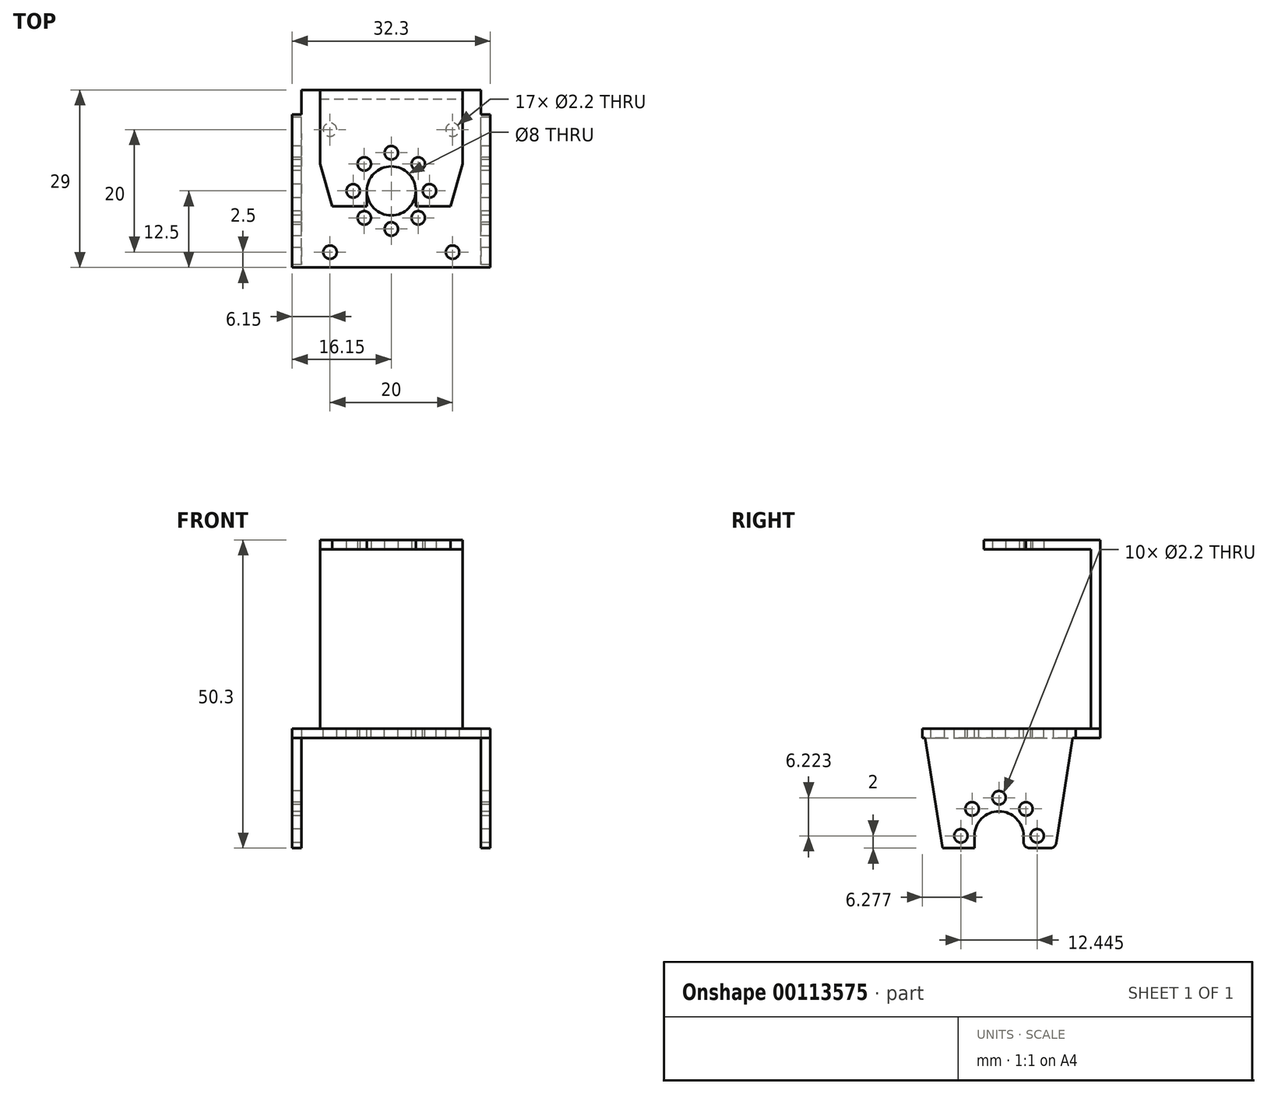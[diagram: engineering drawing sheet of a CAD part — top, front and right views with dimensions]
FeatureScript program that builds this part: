
annotation { "Feature Type Name" : "Feature", "Feature Type Description" : "" }
export const myFeature = defineFeature(function(context is Context, id is Id, definition is map)
    precondition{}
    {
        {
            var Q0;
            Q0=qCreatedBy(makeId("Front.planeOp"),FACE);
            var sketch = newSketch(context, id + "F0", { "sketchPlane" : qUnion([Q0])});
            skLineSegment(sketch, "E0.bottom", {"start": v(0, 0) * mm, "end": v(1.5, 0) * mm});
            skLineSegment(sketch, "E0.top", {"start": v(0, 19.5) * mm, "end": v(32.3, 19.5) * mm});
            skLineSegment(sketch, "E0.left", {"start": v(0, 0) * mm, "end": v(0, 19.5) * mm});
            skLineSegment(sketch, "E0.right", {"start": v(32.3, 0) * mm, "end": v(32.3, 19.5) * mm});
            skLineSegment(sketch, "E1.top", {"start": v(1.5, 18) * mm, "end": v(30.8, 18) * mm});
            skLineSegment(sketch, "E1.left", {"start": v(1.5, 0) * mm, "end": v(1.5, 18) * mm});
            skLineSegment(sketch, "E1.right", {"start": v(30.8, 0) * mm, "end": v(30.8, 18) * mm});
            skLineSegment(sketch, "E2.trimOffspring", {"start": v(30.8, 0) * mm, "end": v(32.3, 0) * mm});
            skSolve(sketch);
        }
        {
            var Q0;
            Q0=qSketchRegion(id+"F0",true);
            extrude(context, id + "F1", {"entities" : qUnion([Q0]), "depth" : 25 * mm});
        }
        {
            var Q0;
            Q0=makeQuery(id+"F1.opExtrude","SWEPT_FACE",FACE,{"disambiguationData":[OSD([sQuery(id+"F0.wireOp",EDGE,"E0.left")])]});
            var sketch = newSketch(context, id + "F2", { "sketchPlane" : qUnion([Q0])});
            skArc(sketch, "E3", {"start": v(16.5, 2) * mm, "mid": v(12.5, 6) * mm, "end": v(8.5, 2) * mm});
            skCircle(sketch, "E4", {"center": v(18.72, 2) * mm, "radius": 1.1 * mm});
            skCircle(sketch, "E5.1.0", {"center": v(16.9, 6.4) * mm, "radius": 1.1 * mm});
            skCircle(sketch, "E5.2.0", {"center": v(12.5, 8.22) * mm, "radius": 1.1 * mm});
            skCircle(sketch, "E5.3.0", {"center": v(8.1, 6.4) * mm, "radius": 1.1 * mm});
            skCircle(sketch, "E5.4.0", {"center": v(6.28, 2) * mm, "radius": 1.1 * mm});
            skLineSegment(sketch, "E6", {"start": v(8.5, 2) * mm, "end": v(8.5, 0) * mm});
            skLineSegment(sketch, "E7", {"start": v(16.5, 2) * mm, "end": v(16.5, 0) * mm});
            skLineSegment(sketch, "E8", {"start": v(8.5, 0) * mm, "end": v(16.5, 0) * mm});
            skLineSegment(sketch, "E9", {"start": v(12.5, 19.5) * mm, "end": v(12.5, 0) * mm, "construction": true});
            skPoint(sketch, "E10", {"position": v(12.5, 0) * mm});
            skLineSegment(sketch, "E11", {"start": v(3.28, 0) * mm, "end": v(0.47, 18) * mm});
            skLineSegment(sketch, "E12", {"start": v(3.28, 0) * mm, "end": v(0, 0) * mm});
            skLineSegment(sketch, "E13", {"start": v(0, 0) * mm, "end": v(0, 18) * mm});
            skLineSegment(sketch, "E14.MirrorCS", {"start": v(25, 0) * mm, "end": v(25, 18) * mm});
            skLineSegment(sketch, "E15.MirrorCS", {"start": v(21.72, 0) * mm, "end": v(24.53, 18) * mm});
            skLineSegment(sketch, "E16.MirrorCS", {"start": v(21.72, 0) * mm, "end": v(25, 0) * mm});
            skLineSegment(sketch, "E17", {"start": v(0, 18) * mm, "end": v(0.47, 18) * mm});
            skPoint(sketch, "E18.orphan", {"position": v(0, 21) * mm});
            skLineSegment(sketch, "E19.MirrorCS", {"start": v(25, 18) * mm, "end": v(24.53, 18) * mm});
            skPoint(sketch, "E20.orphan", {"position": v(25, 21) * mm});
            skSolve(sketch);
        }
        {
            var Q0;
            Q0=qSketchRegion(id+"F2",true);
            extrude(context, id + "F3", {"entities" : qUnion([Q0]), "operationType" : NewBodyOperationType.REMOVE, "endBound" : BoundingType.THROUGH_ALL, "oppositeDirection" : true, "depth" : 25 * mm});
        }
        {
            var Q0;
            Q0=makeQuery(id+"F1.opExtrude","SWEPT_FACE",FACE,{"disambiguationData":[OSD([sQuery(id+"F0.wireOp",EDGE,"E0.top")])]});
            var sketch = newSketch(context, id + "F4", { "sketchPlane" : qUnion([Q0])});
            skLineSegment(sketch, "E21", {"start": v(16.15, 0) * mm, "end": v(16.15, -25) * mm, "construction": true});
            skLineSegment(sketch, "E22", {"start": v(0, -12.5) * mm, "end": v(32.3, -12.5) * mm, "construction": true});
            skCircle(sketch, "E23", {"center": v(6.15, -2.5) * mm, "radius": 1.1 * mm});
            skCircle(sketch, "E24.MirrorC", {"center": v(26.15, -2.5) * mm, "radius": 1.1 * mm});
            skCircle(sketch, "E25.MirrorC", {"center": v(6.15, -22.5) * mm, "radius": 1.1 * mm});
            skCircle(sketch, "E26.MirrorC", {"center": v(26.15, -22.5) * mm, "radius": 1.1 * mm});
            skCircle(sketch, "E27", {"center": v(16.15, -12.5) * mm, "radius": 4 * mm});
            skLineSegment(sketch, "E28.bottom", {"start": v(20.55, -16.9) * mm, "end": v(11.75, -16.9) * mm, "construction": true});
            skLineSegment(sketch, "E28.top", {"start": v(20.55, -8.1) * mm, "end": v(11.75, -8.1) * mm, "construction": true});
            skLineSegment(sketch, "E28.left", {"start": v(20.55, -16.9) * mm, "end": v(20.55, -8.1) * mm, "construction": true});
            skLineSegment(sketch, "E28.right", {"start": v(11.75, -16.9) * mm, "end": v(11.75, -8.1) * mm, "construction": true});
            skCircle(sketch, "E29", {"center": v(11.75, -8.1) * mm, "radius": 1.1 * mm});
            skCircle(sketch, "E30.1.0", {"center": v(9.93, -12.5) * mm, "radius": 1.1 * mm});
            skCircle(sketch, "E30.2.0", {"center": v(11.75, -16.9) * mm, "radius": 1.1 * mm});
            skCircle(sketch, "E30.3.0", {"center": v(16.15, -18.72) * mm, "radius": 1.1 * mm});
            skCircle(sketch, "E31.1.4.0", {"center": v(20.55, -16.9) * mm, "radius": 1.1 * mm});
            skCircle(sketch, "E31.1.5.0", {"center": v(22.37, -12.5) * mm, "radius": 1.1 * mm});
            skCircle(sketch, "E31.1.6.0", {"center": v(20.55, -8.1) * mm, "radius": 1.1 * mm});
            skCircle(sketch, "E31.1.7.0", {"center": v(16.15, -6.28) * mm, "radius": 1.1 * mm});
            skLineSegment(sketch, "E32.0", {"start": v(0, -25) * mm, "end": v(0, 0) * mm, "construction": true});
            skLineSegment(sketch, "E33.0", {"start": v(32.3, -25) * mm, "end": v(32.3, -0.23) * mm, "construction": true});
            skLineSegment(sketch, "E34.0", {"start": v(0, -25) * mm, "end": v(32.3, -25) * mm, "construction": true});
            skPoint(sketch, "E35", {"position": v(16.15, -25) * mm});
            skPoint(sketch, "E36", {"position": v(16.15, 0) * mm});
            skSolve(sketch);
        }
        {
            var Q0;
            Q0=qSketchRegion(id+"F4",true);
            extrude(context, id + "F5", {"entities" : qUnion([Q0]), "operationType" : NewBodyOperationType.REMOVE, "endBound" : BoundingType.UP_TO_NEXT, "oppositeDirection" : true, "depth" : 25 * mm});
        }
        {
            var Q0;
            Q0=makeQuery(id+"F3.boolean.opBoolean","COPY",EDGE,{"disambiguationData":[OD(0.0)],"derivedFrom":makeQuery(id+"F3.opExtrude","SWEPT_EDGE",EDGE,{"disambiguationData":[OSD([sQuery(id+"F0.wireOp",EDGE,"E0.bottom"),sQuery(id+"F0.wireOp",EDGE,"E0.left"),sQuery(id+"F2.wireOp",EDGE,"E11"),sQuery(id+"F2.wireOp",EDGE,"E12")])]})});
            var Q1;
            Q1=makeQuery(id+"F3.boolean.opBoolean","COPY",EDGE,{"disambiguationData":[OD(0.0)],"derivedFrom":makeQuery(id+"F3.opExtrude","SWEPT_EDGE",EDGE,{"disambiguationData":[OSD([sQuery(id+"F0.wireOp",EDGE,"E0.bottom"),sQuery(id+"F0.wireOp",EDGE,"E0.left"),sQuery(id+"F2.wireOp",EDGE,"E6"),sQuery(id+"F2.wireOp",EDGE,"E8")])]})});
            var Q2;
            Q2=makeQuery(id+"F3.boolean.opBoolean","COPY",EDGE,{"disambiguationData":[OD(0.0)],"derivedFrom":makeQuery(id+"F3.opExtrude","SWEPT_EDGE",EDGE,{"disambiguationData":[OSD([sQuery(id+"F0.wireOp",EDGE,"E0.bottom"),sQuery(id+"F0.wireOp",EDGE,"E0.left"),sQuery(id+"F2.wireOp",EDGE,"E7"),sQuery(id+"F2.wireOp",EDGE,"E8")])]})});
            var Q3;
            Q3=makeQuery(id+"F3.boolean.opBoolean","COPY",EDGE,{"disambiguationData":[OD(0.0)],"derivedFrom":makeQuery(id+"F3.opExtrude","SWEPT_EDGE",EDGE,{"disambiguationData":[OSD([sQuery(id+"F0.wireOp",EDGE,"E0.bottom"),sQuery(id+"F0.wireOp",EDGE,"E0.left"),sQuery(id+"F2.wireOp",EDGE,"E15.MirrorCS"),sQuery(id+"F2.wireOp",EDGE,"E16.MirrorCS")])]})});
            var Q4;
            Q4=makeQuery(id+"F3.boolean.opBoolean","COPY",EDGE,{"disambiguationData":[OD(1.0)],"derivedFrom":makeQuery(id+"F3.opExtrude","SWEPT_EDGE",EDGE,{"disambiguationData":[OSD([sQuery(id+"F0.wireOp",EDGE,"E0.bottom"),sQuery(id+"F0.wireOp",EDGE,"E0.left"),sQuery(id+"F2.wireOp",EDGE,"E11"),sQuery(id+"F2.wireOp",EDGE,"E12")])]})});
            var Q5;
            Q5=makeQuery(id+"F3.boolean.opBoolean","COPY",EDGE,{"disambiguationData":[OD(1.0)],"derivedFrom":makeQuery(id+"F3.opExtrude","SWEPT_EDGE",EDGE,{"disambiguationData":[OSD([sQuery(id+"F0.wireOp",EDGE,"E0.bottom"),sQuery(id+"F0.wireOp",EDGE,"E0.left"),sQuery(id+"F2.wireOp",EDGE,"E6"),sQuery(id+"F2.wireOp",EDGE,"E8")])]})});
            var Q6;
            Q6=makeQuery(id+"F3.boolean.opBoolean","COPY",EDGE,{"disambiguationData":[OD(1.0)],"derivedFrom":makeQuery(id+"F3.opExtrude","SWEPT_EDGE",EDGE,{"disambiguationData":[OSD([sQuery(id+"F0.wireOp",EDGE,"E0.bottom"),sQuery(id+"F0.wireOp",EDGE,"E0.left"),sQuery(id+"F2.wireOp",EDGE,"E7"),sQuery(id+"F2.wireOp",EDGE,"E8")])]})});
            var Q7;
            Q7=makeQuery(id+"F3.boolean.opBoolean","COPY",EDGE,{"disambiguationData":[OD(1.0)],"derivedFrom":makeQuery(id+"F3.opExtrude","SWEPT_EDGE",EDGE,{"disambiguationData":[OSD([sQuery(id+"F0.wireOp",EDGE,"E0.bottom"),sQuery(id+"F0.wireOp",EDGE,"E0.left"),sQuery(id+"F2.wireOp",EDGE,"E15.MirrorCS"),sQuery(id+"F2.wireOp",EDGE,"E16.MirrorCS")])]})});
            fillet(context, id + "F6", {"entities" : qUnion([Q0, Q1, Q2, Q3, Q4, Q5, Q6, Q7]), "radius" : 1 * mm, "tangentPropagation" : true, "allowEdgeOverflow" : false});
        }
        {
            var Q0;
            Q0=makeQuery(id+"F1.opExtrude","CAP_FACE",FACE,{"disambiguationData":[OSD([sQuery(id+"F0.wireOp",EDGE,"E0.bottom"),sQuery(id+"F0.wireOp",EDGE,"E0.top"),sQuery(id+"F0.wireOp",EDGE,"E0.left"),sQuery(id+"F0.wireOp",EDGE,"E0.right"),sQuery(id+"F0.wireOp",EDGE,"E1.top"),sQuery(id+"F0.wireOp",EDGE,"E1.left"),sQuery(id+"F0.wireOp",EDGE,"E1.right"),sQuery(id+"F0.wireOp",EDGE,"E2.trimOffspring")])],"isStart":true});
            var sketch = newSketch(context, id + "F7", { "sketchPlane" : qUnion([Q0])});
            skLineSegment(sketch, "E37.bottom", {"start": v(-32.3, 19.5) * mm, "end": v(0, 19.5) * mm});
            skLineSegment(sketch, "E37.top", {"start": v(-32.3, 18) * mm, "end": v(0, 18) * mm});
            skLineSegment(sketch, "E37.left", {"start": v(-32.3, 19.5) * mm, "end": v(-32.3, 18) * mm});
            skLineSegment(sketch, "E37.right", {"start": v(0, 19.5) * mm, "end": v(0, 18) * mm});
            skLineSegment(sketch, "E38", {"start": v(-30.8, 19.5) * mm, "end": v(-30.8, 18) * mm});
            skLineSegment(sketch, "E39", {"start": v(-1.5, 19.5) * mm, "end": v(-1.5, 18) * mm});
            skSolve(sketch);
        }
        {
            var Q0;
            {var subQ0=sQuery(id+"F7.wireOp",EDGE,"E38");Q0=makeQuery(id+"F7.imprint","IMPRINT",FACE,{"disambiguationData":[TD([[makeQuery(id+"F7.imprint","IMPRINT",EDGE,{"derivedFrom":subQ0}),1.0]])]});}
            extrude(context, id + "F8", {"entities" : qUnion([Q0]), "operationType" : NewBodyOperationType.ADD, "depth" : 4 * mm});
        }
        {
            var Q0;
            Q0=makeQuery(id+"F8.boolean.opBoolean","MERGE",FACE,{"derivedFrom":[makeQuery(id+"F1.opExtrude","SWEPT_FACE",FACE,{"disambiguationData":[OSD([sQuery(id+"F0.wireOp",EDGE,"E0.top")])]}),makeQuery(id+"F8.opExtrude","SWEPT_FACE",FACE,{"disambiguationData":[OSD([sQuery(id+"F7.wireOp",EDGE,"E37.bottom")])]})]});
            var sketch = newSketch(context, id + "F9", { "sketchPlane" : qUnion([Q0])});
            skLineSegment(sketch, "E40.bottom", {"start": v(1.5, 4) * mm, "end": v(30.8, 4) * mm});
            skLineSegment(sketch, "E40.top", {"start": v(1.5, 2.5) * mm, "end": v(30.8, 2.5) * mm});
            skLineSegment(sketch, "E40.left", {"start": v(1.5, 4) * mm, "end": v(1.5, 2.5) * mm});
            skLineSegment(sketch, "E40.right", {"start": v(30.8, 4) * mm, "end": v(30.8, 2.5) * mm});
            skSolve(sketch);
        }
        {
            var Q0;
            Q0 = qSketchRegion(id + "F9", true);
            extrude(context, id + "F10", {"entities" : qUnion([Q0]), "operationType" : NewBodyOperationType.ADD, "depth" : (29.3 + 1.5) * mm});
        }
        {
            var Q0;
            Q0=makeQuery(id+"F10.opExtrude","SWEPT_FACE",FACE,{"disambiguationData":[OSD([sQuery(id+"F9.wireOp",EDGE,"E40.top")])]});
            var sketch = newSketch(context, id + "F11", { "sketchPlane" : qUnion([Q0])});
            skLineSegment(sketch, "E41.bottom", {"start": v(1.5, 50.3) * mm, "end": v(30.8, 50.3) * mm});
            skLineSegment(sketch, "E41.top", {"start": v(1.5, 48.8) * mm, "end": v(30.8, 48.8) * mm});
            skLineSegment(sketch, "E41.left", {"start": v(1.5, 50.3) * mm, "end": v(1.5, 48.8) * mm});
            skLineSegment(sketch, "E41.right", {"start": v(30.8, 50.3) * mm, "end": v(30.8, 48.8) * mm});
            skSolve(sketch);
        }
        {
            var Q0;
            Q0 = qSketchRegion(id + "F11", true);
            extrude(context, id + "F12", {"entities" : qUnion([Q0]), "operationType" : NewBodyOperationType.ADD, "depth" : 20 * mm});
        }
        {
            var Q0;
            Q0=makeQuery(id+"F12.opExtrude","SWEPT_FACE",FACE,{"disambiguationData":[OSD([sQuery(id+"F11.wireOp",EDGE,"E41.top")])]});
            var sketch = newSketch(context, id + "F13", { "sketchPlane" : qUnion([Q0])});
            skCircle(sketch, "E42.0", {"center": v(9.93, 12.5) * mm, "radius": 1.1 * mm});
            skCircle(sketch, "E43.0", {"center": v(11.75, 8.1) * mm, "radius": 1.1 * mm});
            skCircle(sketch, "E44.0", {"center": v(16.15, 6.28) * mm, "radius": 1.1 * mm});
            skCircle(sketch, "E45.0", {"center": v(20.55, 8.1) * mm, "radius": 1.1 * mm});
            skCircle(sketch, "E46.0", {"center": v(22.37, 12.5) * mm, "radius": 1.1 * mm});
            skArc(sketch, "E47.0", {"start": v(12.15, 12.5) * mm, "mid": v(16.15, 8.5) * mm, "end": v(20.15, 12.5) * mm});
            skLineSegment(sketch, "E48", {"start": v(12.15, 12.5) * mm, "end": v(12.15, 15) * mm});
            skLineSegment(sketch, "E49", {"start": v(12.15, 15) * mm, "end": v(6.5, 15) * mm});
            skLineSegment(sketch, "E50", {"start": v(16.15, 17.5) * mm, "end": v(16.15, -2.5) * mm, "construction": true});
            skLineSegment(sketch, "E51.MirrorCS", {"start": v(20.15, 12.5) * mm, "end": v(20.15, 15) * mm});
            skLineSegment(sketch, "E52", {"start": v(1.5, 17.5) * mm, "end": v(30.8, 17.5) * mm});
            skLineSegment(sketch, "E53", {"start": v(1.5, -2.5) * mm, "end": v(1.5, 17.5) * mm});
            skLineSegment(sketch, "E54", {"start": v(1.5, -2.5) * mm, "end": v(6.5, 15) * mm});
            skLineSegment(sketch, "E55.MirrorCS", {"start": v(30.8, -2.5) * mm, "end": v(25.8, 15) * mm});
            skLineSegment(sketch, "E56.MirrorCS", {"start": v(30.8, -2.5) * mm, "end": v(30.8, 17.5) * mm});
            skLineSegment(sketch, "E57.MirrorCS", {"start": v(20.15, 15) * mm, "end": v(25.8, 15) * mm});
            skSolve(sketch);
        }
        {
            var Q0;
            Q0 = qSketchRegion(id + "F13", true);
            extrude(context, id + "F14", {"entities" : qUnion([Q0]), "operationType" : NewBodyOperationType.REMOVE, "endBound" : BoundingType.UP_TO_NEXT, "oppositeDirection" : true, "depth" : 25 * mm});
        }
        {
            var Q0;
            Q0=makeQuery(id+"F12.boolean.opBoolean","MERGE",FACE,{"derivedFrom":[makeQuery(id+"F10.opExtrude","CAP_FACE",FACE,{"disambiguationData":[OSD([sQuery(id+"F9.wireOp",EDGE,"E40.bottom"),sQuery(id+"F9.wireOp",EDGE,"E40.top"),sQuery(id+"F9.wireOp",EDGE,"E40.left"),sQuery(id+"F9.wireOp",EDGE,"E40.right")])],"isStart":false}),makeQuery(id+"F12.opExtrude","SWEPT_FACE",FACE,{"disambiguationData":[OSD([sQuery(id+"F11.wireOp",EDGE,"E41.bottom")])]})]});
            var sketch = newSketch(context, id + "F15", { "sketchPlane" : qUnion([Q0])});
            skLineSegment(sketch, "E58", {"start": v(6.5, -15) * mm, "end": v(25.8, -15) * mm, "construction": true});
            skLineSegment(sketch, "E59", {"start": v(16.15, 4) * mm, "end": v(16.15, -15) * mm, "construction": true});
            skPoint(sketch, "E60", {"position": v(11.75, -8.1) * mm});
            skLineSegment(sketch, "E61", {"start": v(4.53, -8.1) * mm, "end": v(4.53, 4) * mm});
            skLineSegment(sketch, "E62.MirrorCS", {"start": v(27.77, -8.1) * mm, "end": v(27.77, 4) * mm});
            skSolve(sketch);
        }
        {
            var Q0;
            {var subQ0=sQuery(id+"F15.wireOp",EDGE,"E61");Q0=makeQuery(id+"F15.imprint","IMPRINT",FACE,{"disambiguationData":[TD([[makeQuery(id+"F15.imprint","IMPRINT",EDGE,{"derivedFrom":subQ0}),1.0]])]});}
            var Q1;
            {var subQ0=sQuery(id+"F15.wireOp",EDGE,"E62.MirrorCS");Q1=makeQuery(id+"F15.imprint","IMPRINT",FACE,{"disambiguationData":[TD([[makeQuery(id+"F15.imprint","IMPRINT",EDGE,{"derivedFrom":subQ0}),-1.0]])]});}
            extrude(context, id + "F16", {"entities" : qUnion([Q0, Q1]), "operationType" : NewBodyOperationType.REMOVE, "oppositeDirection" : true, "depth" : (29.3 + 1.5) * mm});
        }
    });
